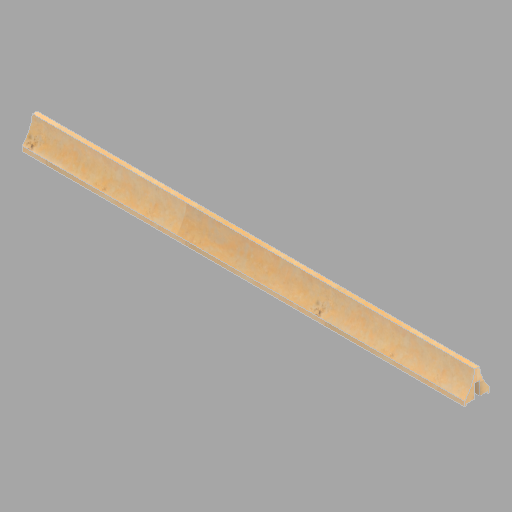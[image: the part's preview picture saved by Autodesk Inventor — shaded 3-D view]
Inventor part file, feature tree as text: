
AUTODESK INVENTOR PART (.ipt)
format: ipt  version: 2022.2 (Build 262287010, 287A)  size: 175,616 bytes
history: native  units: in
note: dims shown in document units (in); Inventor stores cm internally (conversion verified against a paired STEP export)
features: other x1, direct_edit x1, revolve x1
ambient origin geometry x8: Origin, YZ Plane, XZ Plane, XY Plane, X Axis, Y Axis, Z Axis, Center Point
bodies: Solid1 (feature_tree)
feature tree (3):
  other  "North (1)"
  direct_edit  "Direct Edit1"
  revolve  "Rotate1"  [1 undecoded]
note: 1 required parameter value undecoded (feature->parameter linkage not recoverable at this tier; creation-order binding heuristic only, values carry confidence <= 0.55)
